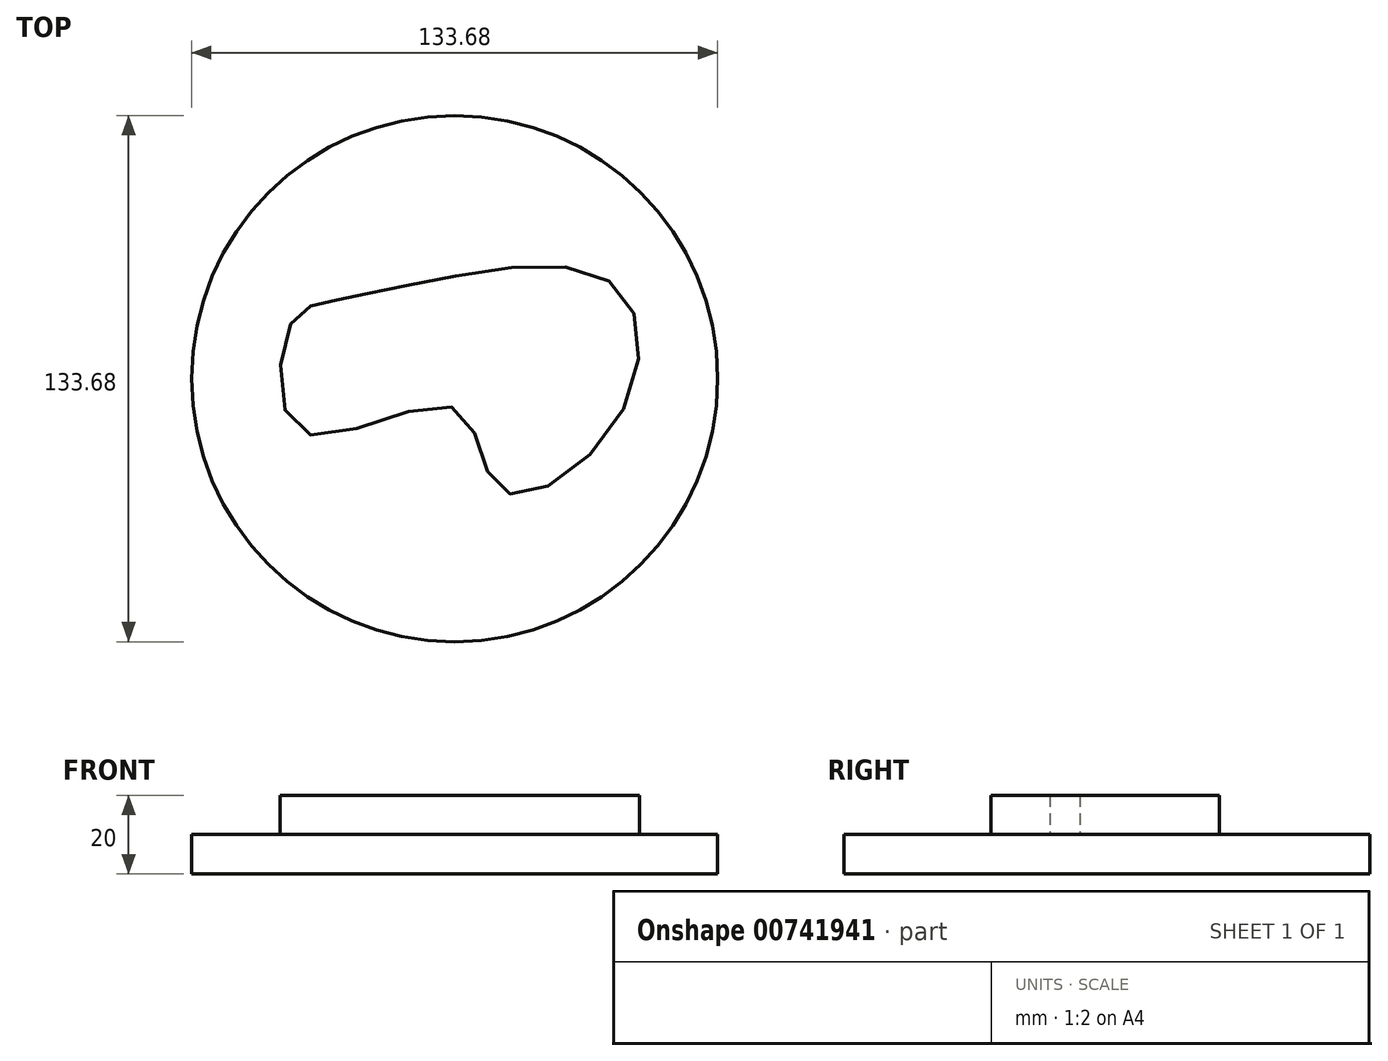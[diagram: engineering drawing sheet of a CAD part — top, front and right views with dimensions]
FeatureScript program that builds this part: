
annotation { "Feature Type Name" : "Feature", "Feature Type Description" : "" }
export const myFeature = defineFeature(function(context is Context, id is Id, definition is map)
    precondition{}
    {
        {
            var Q0;
            Q0=qCreatedBy(makeId("Top.planeOp"),FACE);
            var sketch = newSketch(context, id + "F0", { "sketchPlane" : qUnion([Q0])});
            skCircle(sketch, "E0", {"center": v(0, 0) * mm, "radius": 66.84 * mm});
            skSolve(sketch);
        }
        {
            var Q0;
            Q0=makeQuery(id+"F0.imprint","IMPRINT",FACE,{"disambiguationData":[TD([[makeQuery(id+"F0.imprint","IMPRINT",EDGE,{"derivedFrom":sQuery(id+"F0.wireOp",EDGE,"E0")}),1.0]])]});
            extrude(context, id + "F1", {"entities" : qUnion([Q0]), "depth" : 10 * mm, "offsetDistance" : 25 * mm});
        }
        {
            var Q0;
            Q0=makeQuery(id+"F1.opExtrude","CAP_FACE",FACE,{"disambiguationData":[OSD([sQuery(id+"F0.wireOp",EDGE,"E0")])],"isStart":false});
            var sketch = newSketch(context, id + "F2", { "sketchPlane" : qUnion([Q0])});
            skFitSpline(sketch, "E1", {"points": [v(-41.63, 13.85) * mm, v(-38.56, -13.65) * mm, v(0, -7.5) * mm, v(11.63, -28.27) * mm, v(41.44, -10.38) * mm, v(40.1, 24.23) * mm, v(-6.44, 24.8) * mm, v(-31.25, 19.8) * mm, v(-41.63, 13.85) * mm]});
            skSolve(sketch);
        }
        {
            var Q0;
            Q0=makeQuery(id+"F2.imprint","IMPRINT",FACE,{"disambiguationData":[TD([[makeQuery(id+"F2.imprint","IMPRINT",EDGE,{"derivedFrom":sQuery(id+"F2.wireOp",EDGE,"E1")}),1.0]])]});
            extrude(context, id + "F3", {"entities" : qUnion([Q0]), "operationType" : NewBodyOperationType.ADD, "depth" : 10 * mm, "offsetDistance" : 25 * mm});
        }
    });
